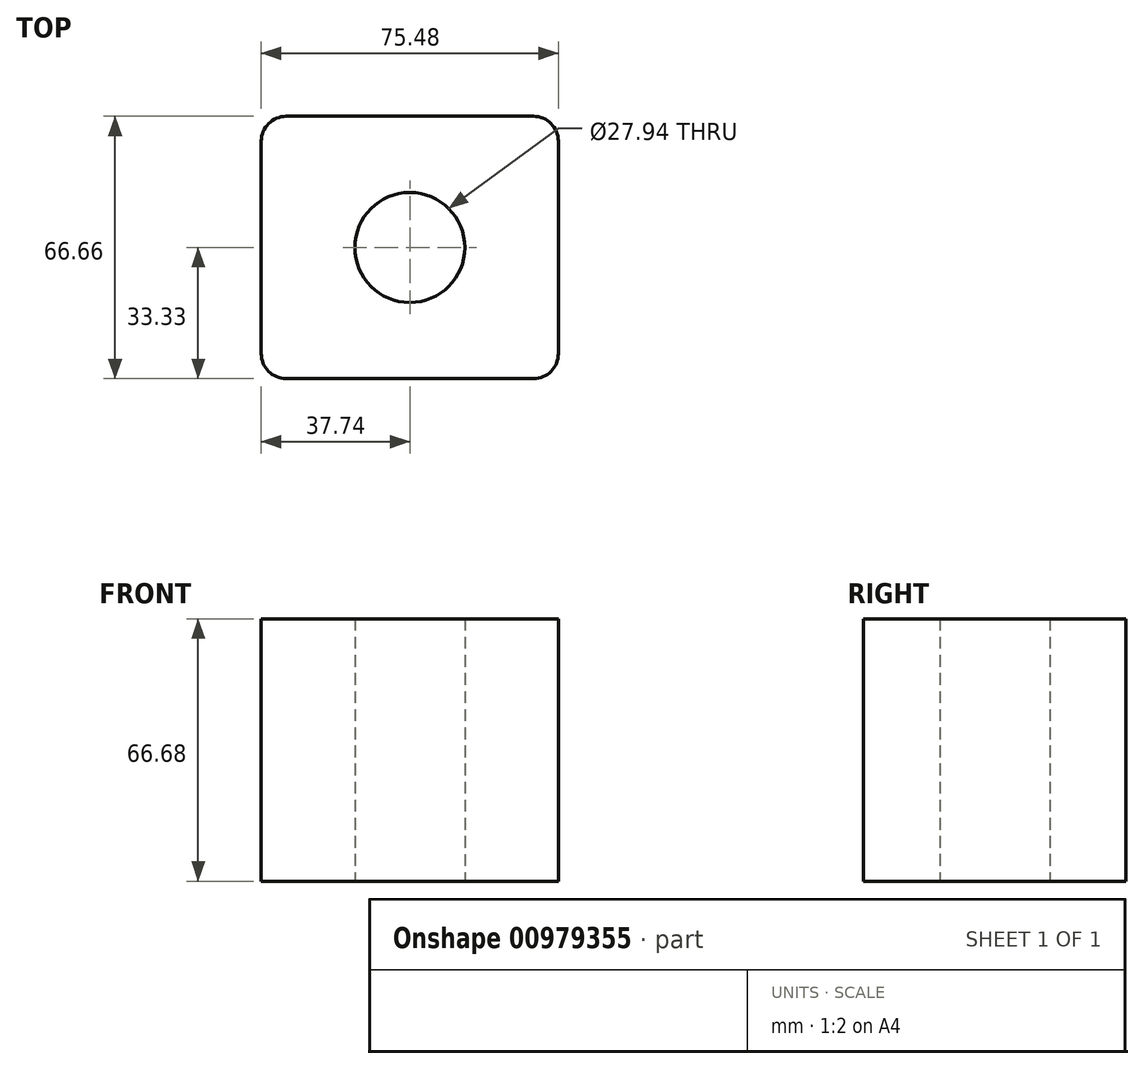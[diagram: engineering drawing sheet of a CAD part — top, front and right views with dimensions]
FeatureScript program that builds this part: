
annotation { "Feature Type Name" : "Feature", "Feature Type Description" : "" }
export const myFeature = defineFeature(function(context is Context, id is Id, definition is map)
    precondition{}
    {
        {
            var Q0;
            Q0=qCreatedBy(makeId("Top.planeOp"),FACE);
            var sketch = newSketch(context, id + "F0", { "sketchPlane" : qUnion([Q0])});
            skLineSegment(sketch, "E0.bottom", {"start": v(31.39, 33.33) * mm, "end": v(-31.39, 33.33) * mm});
            skLineSegment(sketch, "E0.top", {"start": v(31.39, -33.33) * mm, "end": v(-31.39, -33.33) * mm});
            skLineSegment(sketch, "E0.left", {"start": v(37.74, 26.98) * mm, "end": v(37.74, -26.98) * mm});
            skLineSegment(sketch, "E0.right", {"start": v(-37.74, 26.98) * mm, "end": v(-37.74, -26.98) * mm});
            skPoint(sketch, "E0.middle", {"position": v(0, 0) * mm});
            skPoint(sketch, "E1.visualSharp", {"position": v(-37.74, 33.33) * mm});
            skArc(sketch, "E1.filletArc", {"start": v(-31.39, 33.33) * mm, "mid": v(-35.88, 31.47) * mm, "end": v(-37.74, 26.98) * mm});
            skPoint(sketch, "E2.visualSharp", {"position": v(37.74, 33.33) * mm});
            skArc(sketch, "E2.filletArc", {"start": v(37.74, 26.98) * mm, "mid": v(35.88, 31.47) * mm, "end": v(31.39, 33.33) * mm});
            skPoint(sketch, "E3.visualSharp", {"position": v(37.74, -33.33) * mm});
            skArc(sketch, "E3.filletArc", {"start": v(31.39, -33.33) * mm, "mid": v(35.88, -31.47) * mm, "end": v(37.74, -26.98) * mm});
            skPoint(sketch, "E4.visualSharp", {"position": v(-37.74, -33.33) * mm});
            skArc(sketch, "E4.filletArc", {"start": v(-37.74, -26.98) * mm, "mid": v(-35.88, -31.47) * mm, "end": v(-31.39, -33.33) * mm});
            skCircle(sketch, "E5", {"center": v(0, 0) * mm, "radius": 13.97 * mm});
            skSolve(sketch);
        }
        {
            var Q0;
            Q0 = qSketchRegion(id + "F0", true);
            extrude(context, id + "F1", {"entities" : qUnion([Q0]), "depth" : 66.67 * mm, "offsetDistance" : 25.4 * mm});
        }
    });
